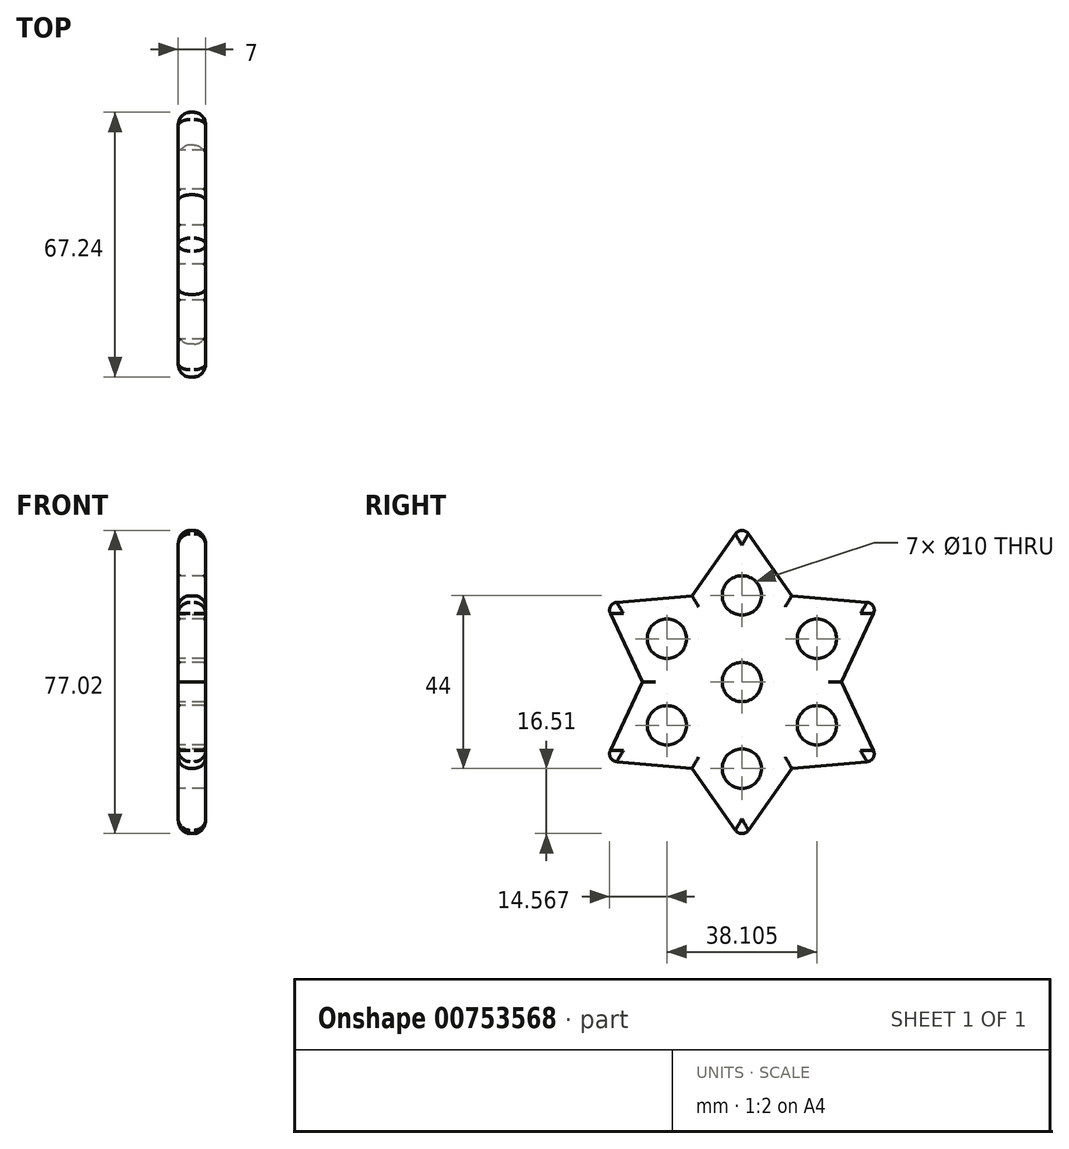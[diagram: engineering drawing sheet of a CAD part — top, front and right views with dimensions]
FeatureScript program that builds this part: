
annotation { "Feature Type Name" : "Feature", "Feature Type Description" : "" }
export const myFeature = defineFeature(function(context is Context, id is Id, definition is map)
    precondition{}
    {
        {
            var Q0;
            Q0=qCreatedBy(makeId("Right.planeOp"),FACE);
            var sketch = newSketch(context, id + "F0", { "sketchPlane" : qUnion([Q0])});
            skPoint(sketch, "E0.center", {"position": v(0, 0) * mm});
            skPoint(sketch, "E1", {"position": v(0, 40) * mm});
            skPoint(sketch, "E2", {"position": v(-12.66, 21.92) * mm});
            skPoint(sketch, "E3", {"position": v(12.66, 21.92) * mm});
            skLineSegment(sketch, "E4", {"start": v(0, 40) * mm, "end": v(12.66, 21.92) * mm});
            skLineSegment(sketch, "E5", {"start": v(0, 40) * mm, "end": v(-12.66, 21.92) * mm});
            skLineSegment(sketch, "E6.1.0", {"start": v(-34.64, 20) * mm, "end": v(-25.31, 0) * mm});
            skLineSegment(sketch, "E6.1.1", {"start": v(-34.64, 20) * mm, "end": v(-12.66, 21.92) * mm});
            skLineSegment(sketch, "E6.2.0", {"start": v(-34.64, -20) * mm, "end": v(-12.66, -21.92) * mm});
            skLineSegment(sketch, "E6.2.1", {"start": v(-34.64, -20) * mm, "end": v(-25.31, 0) * mm});
            skLineSegment(sketch, "E6.3.0", {"start": v(0, -40) * mm, "end": v(12.66, -21.92) * mm});
            skLineSegment(sketch, "E6.3.1", {"start": v(0, -40) * mm, "end": v(-12.66, -21.92) * mm});
            skLineSegment(sketch, "E6.4.0", {"start": v(34.64, -20) * mm, "end": v(25.31, 0) * mm});
            skLineSegment(sketch, "E6.4.1", {"start": v(34.64, -20) * mm, "end": v(12.66, -21.92) * mm});
            skLineSegment(sketch, "E6.5.0", {"start": v(34.64, 20) * mm, "end": v(12.66, 21.92) * mm});
            skLineSegment(sketch, "E6.5.1", {"start": v(34.64, 20) * mm, "end": v(25.31, 0) * mm});
            skLineSegment(sketch, "E7", {"start": v(-12.66, 21.92) * mm, "end": v(12.66, 21.92) * mm, "construction": true});
            skLineSegment(sketch, "E8", {"start": v(-12.66, 40) * mm, "end": v(12.66, 40) * mm, "construction": true});
            skLineSegment(sketch, "E9", {"start": v(0, 40) * mm, "end": v(0, 22) * mm});
            skCircle(sketch, "E10", {"center": v(0, 22) * mm, "radius": 5 * mm});
            skCircle(sketch, "E11.1.0", {"center": v(-19.05, 11) * mm, "radius": 5 * mm});
            skCircle(sketch, "E11.2.0", {"center": v(-19.05, -11) * mm, "radius": 5 * mm});
            skCircle(sketch, "E11.3.0", {"center": v(0, -22) * mm, "radius": 5 * mm});
            skCircle(sketch, "E11.4.0", {"center": v(19.05, -11) * mm, "radius": 5 * mm});
            skCircle(sketch, "E11.5.0", {"center": v(19.05, 11) * mm, "radius": 5 * mm});
            skCircle(sketch, "E12", {"center": v(0, 0) * mm, "radius": 5 * mm});
            skSolve(sketch);
        }
        {
            var Q0;
            Q0=makeQuery(id+"F0.imprint","IMPRINT",FACE,{"disambiguationData":[TD([[makeQuery(id+"F0.imprint","IMPRINT",EDGE,{"derivedFrom":sQuery(id+"F0.wireOp",EDGE,"E4")}),-1.0]])]});
            extrude(context, id + "F1", {"entities" : qUnion([Q0]), "depth" : 7 * mm, "offsetDistance" : 25.4 * mm});
        }
        {
            var Q0;
            Q0=makeQuery(id+"F1.opExtrude","CAP_EDGE",EDGE,{"disambiguationData":[OSD([sQuery(id+"F0.wireOp",EDGE,"E6.1.1")])],"isStart":false});
            var Q1;
            Q1=makeQuery(id+"F1.opExtrude","CAP_EDGE",EDGE,{"disambiguationData":[OSD([sQuery(id+"F0.wireOp",EDGE,"E6.1.0")])],"isStart":false});
            var Q2;
            Q2=makeQuery(id+"F1.opExtrude","CAP_EDGE",EDGE,{"disambiguationData":[OSD([sQuery(id+"F0.wireOp",EDGE,"E6.2.1")])],"isStart":false});
            var Q3;
            Q3=makeQuery(id+"F1.opExtrude","CAP_EDGE",EDGE,{"disambiguationData":[OSD([sQuery(id+"F0.wireOp",EDGE,"E6.2.0")])],"isStart":false});
            var Q4;
            Q4=makeQuery(id+"F1.opExtrude","CAP_EDGE",EDGE,{"disambiguationData":[OSD([sQuery(id+"F0.wireOp",EDGE,"E6.3.1")])],"isStart":false});
            var Q5;
            Q5=makeQuery(id+"F1.opExtrude","CAP_EDGE",EDGE,{"disambiguationData":[OSD([sQuery(id+"F0.wireOp",EDGE,"E6.3.0")])],"isStart":false});
            var Q6;
            Q6=makeQuery(id+"F1.opExtrude","CAP_EDGE",EDGE,{"disambiguationData":[OSD([sQuery(id+"F0.wireOp",EDGE,"E6.4.1")])],"isStart":false});
            var Q7;
            Q7=makeQuery(id+"F1.opExtrude","CAP_EDGE",EDGE,{"disambiguationData":[OSD([sQuery(id+"F0.wireOp",EDGE,"E6.4.0")])],"isStart":false});
            var Q8;
            Q8=makeQuery(id+"F1.opExtrude","CAP_EDGE",EDGE,{"disambiguationData":[OSD([sQuery(id+"F0.wireOp",EDGE,"E6.5.1")])],"isStart":false});
            var Q9;
            Q9=makeQuery(id+"F1.opExtrude","CAP_EDGE",EDGE,{"disambiguationData":[OSD([sQuery(id+"F0.wireOp",EDGE,"E6.5.0")])],"isStart":false});
            var Q10;
            Q10=makeQuery(id+"F1.opExtrude","CAP_EDGE",EDGE,{"disambiguationData":[OSD([sQuery(id+"F0.wireOp",EDGE,"E4")])],"isStart":true});
            var Q11;
            Q11=makeQuery(id+"F1.opExtrude","CAP_EDGE",EDGE,{"disambiguationData":[OSD([sQuery(id+"F0.wireOp",EDGE,"E4")])],"isStart":false});
            var Q12;
            Q12=makeQuery(id+"F1.opExtrude","CAP_EDGE",EDGE,{"disambiguationData":[OSD([sQuery(id+"F0.wireOp",EDGE,"E5")])],"isStart":false});
            var Q13;
            Q13=makeQuery(id+"F1.opExtrude","CAP_EDGE",EDGE,{"disambiguationData":[OSD([sQuery(id+"F0.wireOp",EDGE,"E6.1.0")])],"isStart":true});
            var Q14;
            Q14=makeQuery(id+"F1.opExtrude","CAP_EDGE",EDGE,{"disambiguationData":[OSD([sQuery(id+"F0.wireOp",EDGE,"E6.1.1")])],"isStart":true});
            var Q15;
            Q15=makeQuery(id+"F1.opExtrude","CAP_EDGE",EDGE,{"disambiguationData":[OSD([sQuery(id+"F0.wireOp",EDGE,"E5")])],"isStart":true});
            var Q16;
            Q16=makeQuery(id+"F1.opExtrude","CAP_EDGE",EDGE,{"disambiguationData":[OSD([sQuery(id+"F0.wireOp",EDGE,"E6.5.0")])],"isStart":true});
            var Q17;
            Q17=makeQuery(id+"F1.opExtrude","CAP_EDGE",EDGE,{"disambiguationData":[OSD([sQuery(id+"F0.wireOp",EDGE,"E6.5.1")])],"isStart":true});
            var Q18;
            Q18=makeQuery(id+"F1.opExtrude","CAP_EDGE",EDGE,{"disambiguationData":[OSD([sQuery(id+"F0.wireOp",EDGE,"E6.4.0")])],"isStart":true});
            var Q19;
            Q19=makeQuery(id+"F1.opExtrude","CAP_EDGE",EDGE,{"disambiguationData":[OSD([sQuery(id+"F0.wireOp",EDGE,"E6.4.1")])],"isStart":true});
            var Q20;
            Q20=makeQuery(id+"F1.opExtrude","CAP_EDGE",EDGE,{"disambiguationData":[OSD([sQuery(id+"F0.wireOp",EDGE,"E6.3.0")])],"isStart":true});
            var Q21;
            Q21=makeQuery(id+"F1.opExtrude","CAP_EDGE",EDGE,{"disambiguationData":[OSD([sQuery(id+"F0.wireOp",EDGE,"E6.3.1")])],"isStart":true});
            var Q22;
            Q22=makeQuery(id+"F1.opExtrude","CAP_EDGE",EDGE,{"disambiguationData":[OSD([sQuery(id+"F0.wireOp",EDGE,"E6.2.1")])],"isStart":true});
            var Q23;
            Q23=makeQuery(id+"F1.opExtrude","CAP_EDGE",EDGE,{"disambiguationData":[OSD([sQuery(id+"F0.wireOp",EDGE,"E6.2.0")])],"isStart":true});
            fillet(context, id + "F2", {"entities" : qUnion([Q0, Q1, Q2, Q3, Q4, Q5, Q6, Q7, Q8, Q9, Q10, Q11, Q12, Q13, Q14, Q15, Q16, Q17, Q18, Q19, Q20, Q21, Q22, Q23]), "radius" : 3 * mm, "tangentPropagation" : true, "allowEdgeOverflow" : false});
        }
        {
            var Q0;
            Q0=makeQuery(id+"F2.opFillet","BLEND_EDGE",EDGE,{"blendedFrom":[makeQuery(id+"F1.opExtrude","CAP_EDGE",EDGE,{"disambiguationData":[OSD([sQuery(id+"F0.wireOp",EDGE,"E6.1.0")])],"isStart":false}),makeQuery(id+"F1.opExtrude","CAP_EDGE",EDGE,{"disambiguationData":[OSD([sQuery(id+"F0.wireOp",EDGE,"E6.1.1")])],"isStart":false})],"blendedInto":[]});
            var Q1;
            Q1=makeQuery(id+"F2.opFillet","BLEND_EDGE",EDGE,{"blendedFrom":[makeQuery(id+"F1.opExtrude","CAP_EDGE",EDGE,{"disambiguationData":[OSD([sQuery(id+"F0.wireOp",EDGE,"E4")])],"isStart":false}),makeQuery(id+"F1.opExtrude","CAP_EDGE",EDGE,{"disambiguationData":[OSD([sQuery(id+"F0.wireOp",EDGE,"E5")])],"isStart":false})],"blendedInto":[]});
            var Q2;
            Q2=makeQuery(id+"F2.opFillet","BLEND_EDGE",EDGE,{"blendedFrom":[makeQuery(id+"F1.opExtrude","CAP_EDGE",EDGE,{"disambiguationData":[OSD([sQuery(id+"F0.wireOp",EDGE,"E6.1.0")])],"isStart":true}),makeQuery(id+"F1.opExtrude","CAP_EDGE",EDGE,{"disambiguationData":[OSD([sQuery(id+"F0.wireOp",EDGE,"E6.1.1")])],"isStart":true})],"blendedInto":[]});
            var Q3;
            Q3=makeQuery(id+"F2.opFillet","BLEND_EDGE",EDGE,{"blendedFrom":[makeQuery(id+"F1.opExtrude","CAP_EDGE",EDGE,{"disambiguationData":[OSD([sQuery(id+"F0.wireOp",EDGE,"E6.2.0")])],"isStart":false}),makeQuery(id+"F1.opExtrude","CAP_EDGE",EDGE,{"disambiguationData":[OSD([sQuery(id+"F0.wireOp",EDGE,"E6.2.1")])],"isStart":false})],"blendedInto":[]});
            var Q4;
            Q4=makeQuery(id+"F2.opFillet","BLEND_EDGE",EDGE,{"blendedFrom":[makeQuery(id+"F1.opExtrude","CAP_EDGE",EDGE,{"disambiguationData":[OSD([sQuery(id+"F0.wireOp",EDGE,"E6.3.0")])],"isStart":false}),makeQuery(id+"F1.opExtrude","CAP_EDGE",EDGE,{"disambiguationData":[OSD([sQuery(id+"F0.wireOp",EDGE,"E6.3.1")])],"isStart":false})],"blendedInto":[]});
            var Q5;
            Q5=makeQuery(id+"F2.opFillet","BLEND_EDGE",EDGE,{"blendedFrom":[makeQuery(id+"F1.opExtrude","CAP_EDGE",EDGE,{"disambiguationData":[OSD([sQuery(id+"F0.wireOp",EDGE,"E6.2.0")])],"isStart":true}),makeQuery(id+"F1.opExtrude","CAP_EDGE",EDGE,{"disambiguationData":[OSD([sQuery(id+"F0.wireOp",EDGE,"E6.2.1")])],"isStart":true})],"blendedInto":[]});
            var Q6;
            Q6=makeQuery(id+"F2.opFillet","BLEND_EDGE",EDGE,{"blendedFrom":[makeQuery(id+"F1.opExtrude","CAP_EDGE",EDGE,{"disambiguationData":[OSD([sQuery(id+"F0.wireOp",EDGE,"E6.3.0")])],"isStart":true}),makeQuery(id+"F1.opExtrude","CAP_EDGE",EDGE,{"disambiguationData":[OSD([sQuery(id+"F0.wireOp",EDGE,"E6.3.1")])],"isStart":true})],"blendedInto":[]});
            var Q7;
            Q7=makeQuery(id+"F2.opFillet","BLEND_EDGE",EDGE,{"blendedFrom":[makeQuery(id+"F1.opExtrude","CAP_EDGE",EDGE,{"disambiguationData":[OSD([sQuery(id+"F0.wireOp",EDGE,"E6.4.0")])],"isStart":false}),makeQuery(id+"F1.opExtrude","CAP_EDGE",EDGE,{"disambiguationData":[OSD([sQuery(id+"F0.wireOp",EDGE,"E6.4.1")])],"isStart":false})],"blendedInto":[]});
            var Q8;
            Q8=makeQuery(id+"F2.opFillet","BLEND_EDGE",EDGE,{"blendedFrom":[makeQuery(id+"F1.opExtrude","CAP_EDGE",EDGE,{"disambiguationData":[OSD([sQuery(id+"F0.wireOp",EDGE,"E6.5.0")])],"isStart":false}),makeQuery(id+"F1.opExtrude","CAP_EDGE",EDGE,{"disambiguationData":[OSD([sQuery(id+"F0.wireOp",EDGE,"E6.5.1")])],"isStart":false})],"blendedInto":[]});
            var Q9;
            Q9=makeQuery(id+"F2.opFillet","BLEND_EDGE",EDGE,{"blendedFrom":[makeQuery(id+"F1.opExtrude","CAP_EDGE",EDGE,{"disambiguationData":[OSD([sQuery(id+"F0.wireOp",EDGE,"E6.4.0")])],"isStart":true}),makeQuery(id+"F1.opExtrude","CAP_EDGE",EDGE,{"disambiguationData":[OSD([sQuery(id+"F0.wireOp",EDGE,"E6.4.1")])],"isStart":true})],"blendedInto":[]});
            var Q10;
            Q10=makeQuery(id+"F2.opFillet","BLEND_EDGE",EDGE,{"blendedFrom":[makeQuery(id+"F1.opExtrude","CAP_EDGE",EDGE,{"disambiguationData":[OSD([sQuery(id+"F0.wireOp",EDGE,"E6.5.0")])],"isStart":true}),makeQuery(id+"F1.opExtrude","CAP_EDGE",EDGE,{"disambiguationData":[OSD([sQuery(id+"F0.wireOp",EDGE,"E6.5.1")])],"isStart":true})],"blendedInto":[]});
            fillet(context, id + "F3", {"entities" : qUnion([Q0, Q1, Q2, Q3, Q4, Q5, Q6, Q7, Q8, Q9, Q10]), "radius" : 2 * mm, "tangentPropagation" : true, "allowEdgeOverflow" : false});
        }
        {
            var Q0;
            Q0=makeQuery(id+"F1.opExtrude","CAP_EDGE",EDGE,{"disambiguationData":[OSD([sQuery(id+"F0.wireOp",EDGE,"E10")])],"isStart":false});
            var Q1;
            Q1=makeQuery(id+"F1.opExtrude","CAP_EDGE",EDGE,{"disambiguationData":[OSD([sQuery(id+"F0.wireOp",EDGE,"E11.1.0")])],"isStart":false});
            var Q2;
            Q2=makeQuery(id+"F1.opExtrude","CAP_EDGE",EDGE,{"disambiguationData":[OSD([sQuery(id+"F0.wireOp",EDGE,"E11.2.0")])],"isStart":false});
            var Q3;
            Q3=makeQuery(id+"F1.opExtrude","CAP_EDGE",EDGE,{"disambiguationData":[OSD([sQuery(id+"F0.wireOp",EDGE,"E11.3.0")])],"isStart":false});
            var Q4;
            Q4=makeQuery(id+"F1.opExtrude","CAP_EDGE",EDGE,{"disambiguationData":[OSD([sQuery(id+"F0.wireOp",EDGE,"E11.4.0")])],"isStart":false});
            var Q5;
            Q5=makeQuery(id+"F1.opExtrude","CAP_EDGE",EDGE,{"disambiguationData":[OSD([sQuery(id+"F0.wireOp",EDGE,"E11.5.0")])],"isStart":false});
            var Q6;
            Q6=makeQuery(id+"F1.opExtrude","CAP_EDGE",EDGE,{"disambiguationData":[OSD([sQuery(id+"F0.wireOp",EDGE,"E11.4.0")])],"isStart":true});
            var Q7;
            Q7=makeQuery(id+"F1.opExtrude","CAP_EDGE",EDGE,{"disambiguationData":[OSD([sQuery(id+"F0.wireOp",EDGE,"E11.5.0")])],"isStart":true});
            var Q8;
            Q8=makeQuery(id+"F1.opExtrude","CAP_EDGE",EDGE,{"disambiguationData":[OSD([sQuery(id+"F0.wireOp",EDGE,"E11.3.0")])],"isStart":true});
            var Q9;
            Q9=makeQuery(id+"F1.opExtrude","CAP_EDGE",EDGE,{"disambiguationData":[OSD([sQuery(id+"F0.wireOp",EDGE,"E11.2.0")])],"isStart":true});
            var Q10;
            Q10=makeQuery(id+"F1.opExtrude","CAP_EDGE",EDGE,{"disambiguationData":[OSD([sQuery(id+"F0.wireOp",EDGE,"E11.1.0")])],"isStart":true});
            var Q11;
            Q11=makeQuery(id+"F1.opExtrude","CAP_EDGE",EDGE,{"disambiguationData":[OSD([sQuery(id+"F0.wireOp",EDGE,"E10")])],"isStart":true});
            var Q12;
            Q12=makeQuery(id+"F1.opExtrude","CAP_EDGE",EDGE,{"disambiguationData":[OSD([sQuery(id+"F0.wireOp",EDGE,"E12")])],"isStart":true});
            var Q13;
            Q13=makeQuery(id+"F1.opExtrude","CAP_EDGE",EDGE,{"disambiguationData":[OSD([sQuery(id+"F0.wireOp",EDGE,"E12")])],"isStart":false});
            fillet(context, id + "F4", {"entities" : qUnion([Q0, Q1, Q2, Q3, Q4, Q5, Q6, Q7, Q8, Q9, Q10, Q11, Q12, Q13]), "radius" : 0.5 * mm, "tangentPropagation" : true, "allowEdgeOverflow" : false});
        }
    });
